# Revit family: VIESSMANN - Energycal AW Pro AT DWS
name_source: partatom
category: Wyposażenie mechaniczne
revit_build: Autodesk Revit 2017 (Build: 20160720_1515(x64)
units: mm (PartAtom-declared; Revit-internal decimal feet)

## family parameters
Numer OmniClass = 23.75.10.21.11
Oparty na płaszczyźnie roboczej = Nie
Punkt obliczania pomieszczeń = Nie
Tnij formami wycięć po wczytaniu = Nie
Typ części = Normalny
Tytuł OmniClass = Air-Source Heat Pumps
Współdzielony = Nie
Wymiar okrągłego złącza = Użyj średnicy
Zawsze pionowo = Tak

## types (5) — shared parameters
Autor = www.archispace.pl
Częstotliwość = 50 Hz
Długość całkowita = 1403 mm  [stored 4.60302 ft]
Ilość/Obiegi chłodnicze sprężarki (nr/nr) = 2/1
Klasa efektywności praca niskotemperaturowa (A7W35) = A
Liczba biegunów = 3
Liczba wentylatorów = 1
Liczba wymienników = 1
Moc nominalna silnika pompy obiegowej = 1 kW
Moc nominalna wentylatora = 2 kW
Model = Powietrzna pompa ciepła Energycal AW PRO AT / Air-water heat pump Energycal AW PRO AT DWS
Model pompy = P1
Opis = Energycal AW Pro AT jest kompletną, dedykowaną serią rewersyjnych dwustopniowych pomp ciepła powietrze-woda, o zakresie mocy od 40 do 74 kW, wykorzystującą czynnik chłodniczy (R410A).
Producent = Viessmann Sp. z o.o
Prąd nominalny silnika pompy obiegowej = 3 A
Prąd nominalny wentylatora = 4 A
Stopień wydajności = 0-50-100%
Szerokość całkowita = 1791 mm  [stored 5.87598 ft]
Typ sprężarki = Spiralna
Typ wentylatora = Osiowy
Typ wymiennika po stronie użytkowej = Płytowy
URL = https://www.viessmann-projektant.pl
Viessmann Kolor 1 = Viessmann Kolor 2
Viessmann Kolor 2 = Viessmann Kolor 3
Współczynnik mocy = 1
Wysokość całkowita = 2390 mm  [stored 7.84121 ft]
Zasilanie elektryczne (V/ph/Hz) = 400/3~/50
Zasilanie opcjonalne (V/ph/Hz) = 230/1~/50
Średnica1 = 1 1/2"
Średnica2 = 2"

## per-type parameters (varying)
- Wielkość jednostki - 50: Całkowite napełnienie czynnikiem chłodniczym=14.00 kg; Całkowite napełnienie olejem=3.80 kg; Ciężar=575.00 kg; Maksymalna moc pobierania=20 kW; Maksymalna moc pobierania (z pompą obiegową)=22 kW; Maksymalny pobór prądu=36 A; Maksymalny pobór prądu (z pompą obiegową)=39 A; Maksymalny prąd rozruchowy=121 A; Maksymalny prąd rozruchowy (z pompą obiegową i funkcją Soft-Starter)=83 A; Maksymalny prąd rozruchowy (z pompą obiegową)=124 A; Maksymalny prąd rozruchowy z układem Soft-Starter=81 A; Napięcie zasilania=400 V; Natężenie przepływu wody (A7W35)=1.9 L/s; Natężenie przepływu wody (A7W35) l/h=6948; Nominalna wydajność grzewcza (A7W35)=40 kW; Obciążenie pozorne=20200 VA; Pobór mocy elektrycznej (A7W35)=10 kW; Pojemność wodna=5.2 L; Poziom ciśnienia akustycznego - wersja cicha LN dB(A)=53 mm  [stored 0.173885 ft]; Poziom ciśnienia akustycznego - wersja super cicha SLN dB(A)=50 mm  [stored 0.164042 ft]; Poziom ciśnienia akustycznego dB(A)=55 mm  [stored 0.180446 ft]; Poziom mocy akustycznej - wersja cicha LN dB(A)=81 mm  [stored 0.265748 ft]; Poziom mocy akustycznej - wersja super cicha SLN dB(A)=78 mm  [stored 0.255906 ft]; Poziom mocy akustycznej dB(A)=83 mm  [stored 0.27231 ft]; Przepływ powietrza=17000.0 m³/h; Spadek ciśnienia wody (A7W35)=30.0 kPa; Użyteczna wysokość podnoszenia pompy=167.0 kPa; Współczynnik wydajności [COP] (A7W35)=4.14
- Wielkość jednostki - 60: Całkowite napełnienie czynnikiem chłodniczym=18.00 kg; Całkowite napełnienie olejem=6.80 kg; Ciężar=592.00 kg; Maksymalna moc pobierania=24 kW; Maksymalna moc pobierania (z pompą obiegową)=25 kW; Maksymalny pobór prądu=41 A; Maksymalny pobór prądu (z pompą obiegową)=44 A; Maksymalny prąd rozruchowy=151 A; Maksymalny prąd rozruchowy (z pompą obiegową i funkcją Soft-Starter)=101 A; Maksymalny prąd rozruchowy (z pompą obiegową)=153 A; Maksymalny prąd rozruchowy z układem Soft-Starter=103 A; Napięcie zasilania=0 V; Natężenie przepływu wody (A7W35)=2.4 L/s; Natężenie przepływu wody (A7W35) l/h=8461; Nominalna wydajność grzewcza (A7W35)=49 kW; Obciążenie pozorne=23800 VA; Pobór mocy elektrycznej (A7W35)=12 kW; Pojemność wodna=6.5 L; Poziom ciśnienia akustycznego - wersja cicha LN dB(A)=53 mm  [stored 0.173885 ft]; Poziom ciśnienia akustycznego - wersja super cicha SLN dB(A)=50 mm  [stored 0.164042 ft]; Poziom ciśnienia akustycznego dB(A)=55 mm  [stored 0.180446 ft]; Poziom mocy akustycznej - wersja cicha LN dB(A)=81 mm  [stored 0.265748 ft]; Poziom mocy akustycznej - wersja super cicha SLN dB(A)=78 mm  [stored 0.255906 ft]; Poziom mocy akustycznej dB(A)=83 mm  [stored 0.27231 ft]; Przepływ powietrza=18500.0 m³/h; Spadek ciśnienia wody (A7W35)=33.0 kPa; Użyteczna wysokość podnoszenia pompy=160.0 kPa; Współczynnik wydajności [COP] (A7W35)=4.26
- Wielkość jednostki - 70: Całkowite napełnienie czynnikiem chłodniczym=19.00 kg; Całkowite napełnienie olejem=6.80 kg; Ciężar=602.00 kg; Maksymalna moc pobierania=28 kW; Maksymalna moc pobierania (z pompą obiegową)=29 kW; Maksymalny pobór prądu=46 A; Maksymalny pobór prądu (z pompą obiegową)=49 A; Maksymalny prąd rozruchowy=143 A; Maksymalny prąd rozruchowy (z pompą obiegową i funkcją Soft-Starter)=96 A; Maksymalny prąd rozruchowy (z pompą obiegową)=146 A; Maksymalny prąd rozruchowy z układem Soft-Starter=98 A; Napięcie zasilania=0 V; Natężenie przepływu wody (A7W35)=2.6 L/s; Natężenie przepływu wody (A7W35) l/h=9475; Nominalna wydajność grzewcza (A7W35)=55 kW; Obciążenie pozorne=27700 VA; Pobór mocy elektrycznej (A7W35)=13 kW; Pojemność wodna=7.8 L; Poziom ciśnienia akustycznego - wersja cicha LN dB(A)=54 mm  [stored 0.177165 ft]; Poziom ciśnienia akustycznego - wersja super cicha SLN dB(A)=51 mm; Poziom ciśnienia akustycznego dB(A)=56 mm  [stored 0.183727 ft]; Poziom mocy akustycznej - wersja cicha LN dB(A)=82 mm  [stored 0.269029 ft]; Poziom mocy akustycznej - wersja super cicha SLN dB(A)=79 mm; Poziom mocy akustycznej dB(A)=84 mm  [stored 0.275591 ft]; Przepływ powietrza=18500.0 m³/h; Spadek ciśnienia wody (A7W35)=31.0 kPa; Użyteczna wysokość podnoszenia pompy=159.0 kPa; Współczynnik wydajności [COP] (A7W35)=4.12
- Wielkość jednostki - 80: Całkowite napełnienie czynnikiem chłodniczym=23.00 kg; Całkowite napełnienie olejem=6.80 kg; Ciężar=620.00 kg; Maksymalna moc pobierania=32 kW; Maksymalna moc pobierania (z pompą obiegową)=34 kW; Maksymalny pobór prądu=56 A; Maksymalny pobór prądu (z pompą obiegową)=59 A; Maksymalny prąd rozruchowy=170 A; Maksymalny prąd rozruchowy (z pompą obiegową i funkcją Soft-Starter)=114 A; Maksymalny prąd rozruchowy (z pompą obiegową)=173 A; Maksymalny prąd rozruchowy z układem Soft-Starter=116 A; Napięcie zasilania=400 V; Natężenie przepływu wody (A7W35)=3.2 L/s; Natężenie przepływu wody (A7W35) l/h=11694; Nominalna wydajność grzewcza (A7W35)=68 kW; Obciążenie pozorne=32400 VA; Pobór mocy elektrycznej (A7W35)=16 kW; Pojemność wodna=9.1 L; Poziom ciśnienia akustycznego - wersja cicha LN dB(A)=55 mm  [stored 0.180446 ft]; Poziom ciśnienia akustycznego - wersja super cicha SLN dB(A)=0 mm  [stored 0 ft]; Poziom ciśnienia akustycznego dB(A)=57 mm  [stored 0.187008 ft]; Poziom mocy akustycznej - wersja cicha LN dB(A)=83 mm  [stored 0.27231 ft]; Poziom mocy akustycznej - wersja super cicha SLN dB(A)=0 mm  [stored 0 ft]; Poziom mocy akustycznej dB(A)=85 mm  [stored 0.278871 ft]; Przepływ powietrza=21000.0 m³/h; Spadek ciśnienia wody (A7W35)=35.0 kPa; Użyteczna wysokość podnoszenia pompy=146.0 kPa; Współczynnik wydajności [COP] (A7W35)=4.19
- Wielkość jednostki - 90: Całkowite napełnienie czynnikiem chłodniczym=23.00 kg; Całkowite napełnienie olejem=6.80 kg; Ciężar=631.00 kg; Maksymalna moc pobierania=38 kW; Maksymalna moc pobierania (z pompą obiegową)=40 kW; Maksymalny pobór prądu=75 A; Maksymalny pobór prądu (z pompą obiegową)=77 A; Maksymalny prąd rozruchowy=213 A; Maksymalny prąd rozruchowy (z pompą obiegową i funkcją Soft-Starter)=143 A; Maksymalny prąd rozruchowy (z pompą obiegową)=216 A; Maksymalny prąd rozruchowy z układem Soft-Starter=145 A; Napięcie zasilania=400 V; Natężenie przepływu wody (A7W35)=3.6 L/s; Natężenie przepływu wody (A7W35) l/h=12794; Nominalna wydajność grzewcza (A7W35)=74 kW; Obciążenie pozorne=38100 VA; Pobór mocy elektrycznej (A7W35)=13 kW; Pojemność wodna=10.4 L; Poziom ciśnienia akustycznego - wersja cicha LN dB(A)=55 mm  [stored 0.180446 ft]; Poziom ciśnienia akustycznego - wersja super cicha SLN dB(A)=0 mm  [stored 0 ft]; Poziom ciśnienia akustycznego dB(A)=57 mm  [stored 0.187008 ft]; Poziom mocy akustycznej - wersja cicha LN dB(A)=83 mm  [stored 0.27231 ft]; Poziom mocy akustycznej - wersja super cicha SLN dB(A)=0 mm  [stored 0 ft]; Poziom mocy akustycznej dB(A)=85 mm  [stored 0.278871 ft]; Przepływ powietrza=21000.0 m³/h; Spadek ciśnienia wody (A7W35)=34.0 kPa; Użyteczna wysokość podnoszenia pompy=142.0 kPa; Współczynnik wydajności [COP] (A7W35)=4.12

note: [stored X ft] marks values corroborated as IEEE doubles in the binary element streams (Revit-internal decimal feet)
